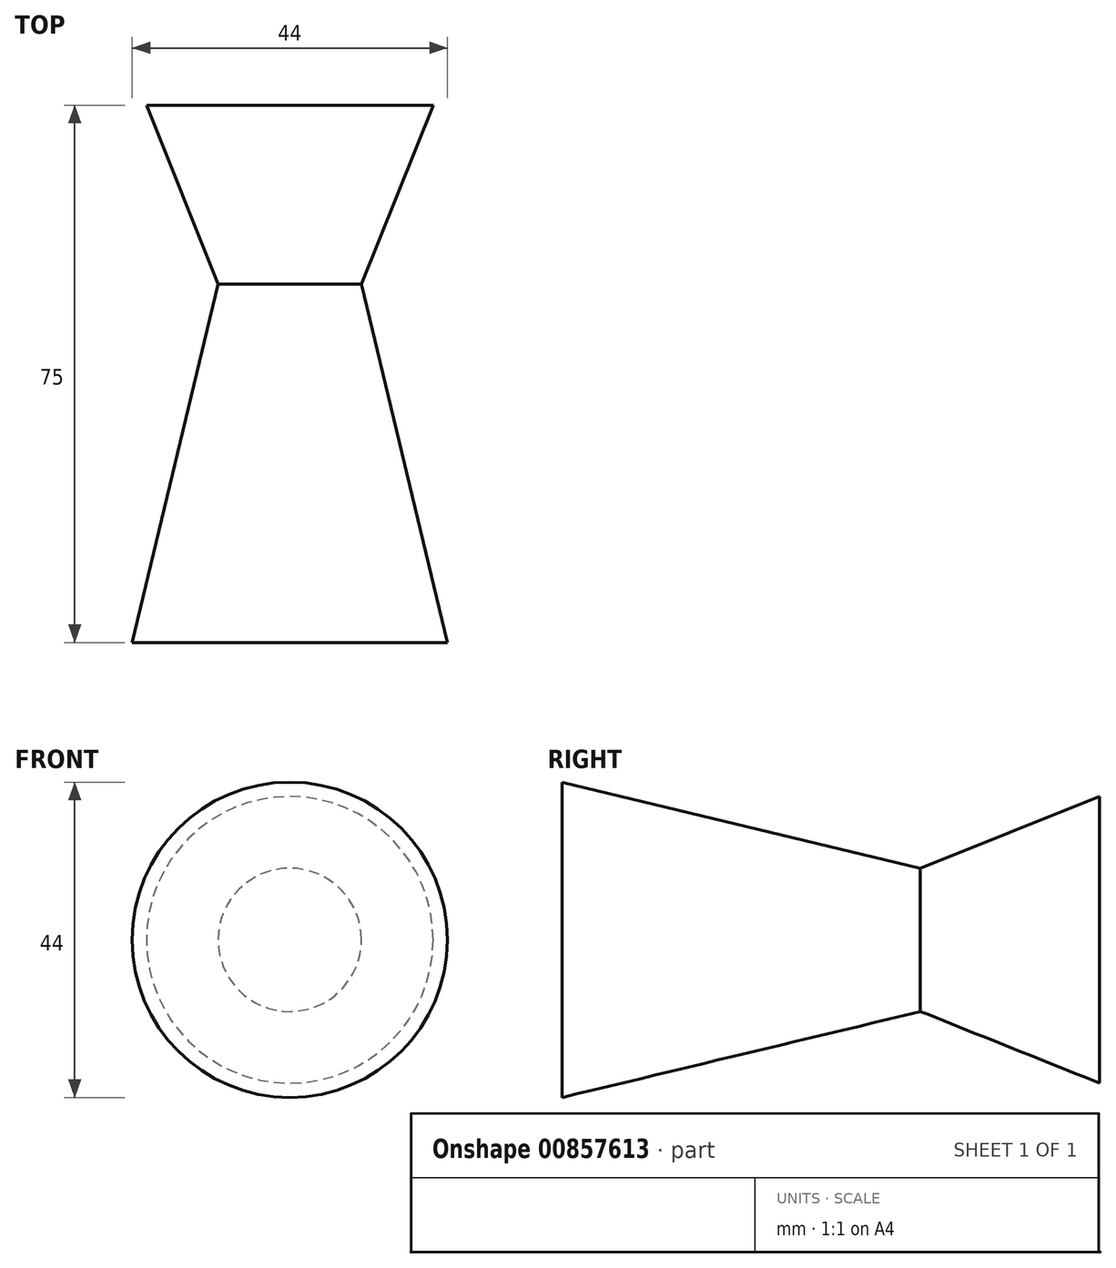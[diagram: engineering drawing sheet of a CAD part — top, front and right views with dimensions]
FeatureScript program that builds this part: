
annotation { "Feature Type Name" : "Feature", "Feature Type Description" : "" }
export const myFeature = defineFeature(function(context is Context, id is Id, definition is map)
    precondition{}
    {
        {
            var Q0;
            Q0=qCreatedBy(makeId("Right.planeOp"),FACE);
            var sketch = newSketch(context, id + "F0", { "sketchPlane" : qUnion([Q0])});
            skLineSegment(sketch, "E0", {"start": v(25, 20) * mm, "end": v(25, 0) * mm});
            skLineSegment(sketch, "E1", {"start": v(-50, 0) * mm, "end": v(-50, 22) * mm});
            skLineSegment(sketch, "E2", {"start": v(0, 0) * mm, "end": v(0, 10) * mm});
            skLineSegment(sketch, "E3", {"start": v(-50, 0) * mm, "end": v(0, 0) * mm});
            skLineSegment(sketch, "E4", {"start": v(0, 0) * mm, "end": v(25, 0) * mm});
            skLineSegment(sketch, "E5", {"start": v(-50, 22) * mm, "end": v(0, 10) * mm});
            skLineSegment(sketch, "E6", {"start": v(25, 20) * mm, "end": v(0, 10) * mm});
            skSolve(sketch);
        }
        {
            var Q0;
            Q0 = qSketchRegion(id + "F0", true);
            var Q1;
            Q1=sQuery(id+"F0.wireOp",EDGE,"E3");
            revolve(context, id + "F1", {"surfaceOperationType" : NewSurfaceOperationType.NEW, "entities" : qUnion([Q0]), "axis" : qUnion([Q1]), "revolveType" : RevolveType.FULL});
        }
    });
